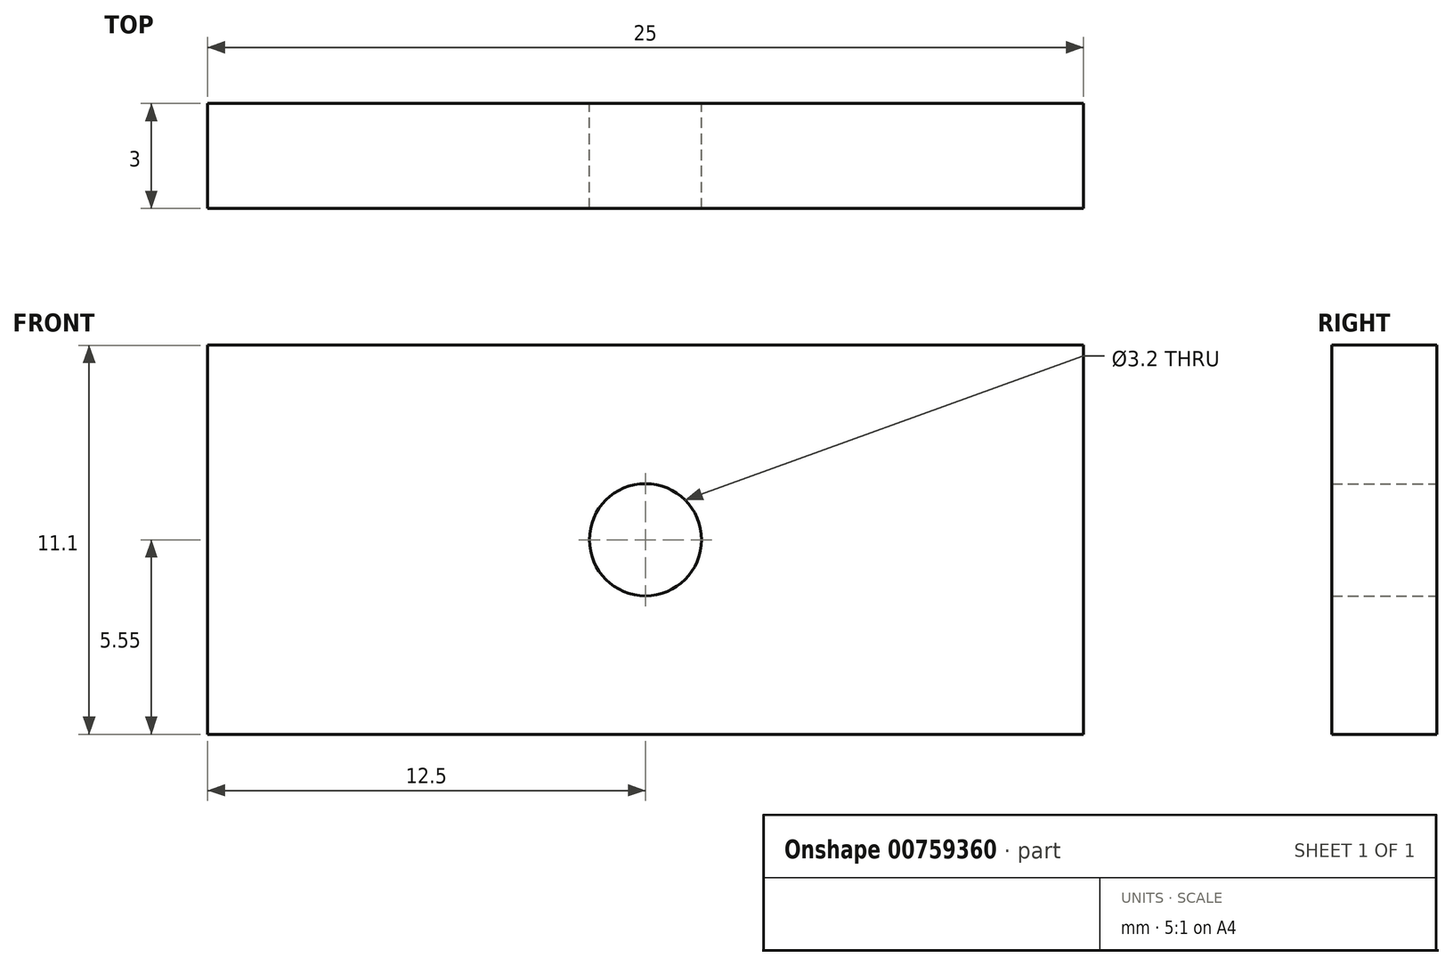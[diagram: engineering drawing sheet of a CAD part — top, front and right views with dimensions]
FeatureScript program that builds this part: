
annotation { "Feature Type Name" : "Feature", "Feature Type Description" : "" }
export const myFeature = defineFeature(function(context is Context, id is Id, definition is map)
    precondition{}
    {
        {
            var Q0;
            Q0=qCreatedBy(makeId("Front.planeOp"),FACE);
            var sketch = newSketch(context, id + "F0", { "sketchPlane" : qUnion([Q0])});
            skLineSegment(sketch, "E0.bottom", {"start": v(-12.5, 5.56) * mm, "end": v(12.5, 5.56) * mm});
            skLineSegment(sketch, "E0.top", {"start": v(-12.5, -5.56) * mm, "end": v(12.5, -5.56) * mm});
            skLineSegment(sketch, "E0.left", {"start": v(-12.5, 5.56) * mm, "end": v(-12.5, -5.56) * mm});
            skLineSegment(sketch, "E0.right", {"start": v(12.5, 5.56) * mm, "end": v(12.5, -5.56) * mm});
            skPoint(sketch, "E0.middle", {"position": v(0, 0) * mm});
            skCircle(sketch, "E1", {"center": v(0, 0) * mm, "radius": 1.6 * mm});
            skSolve(sketch);
        }
        {
            var Q0;
            Q0 = qSketchRegion(id + "F0", true);
            extrude(context, id + "F1", {"entities" : qUnion([Q0]), "depth" : 3 * mm, "offsetDistance" : 25 * mm});
        }
    });
